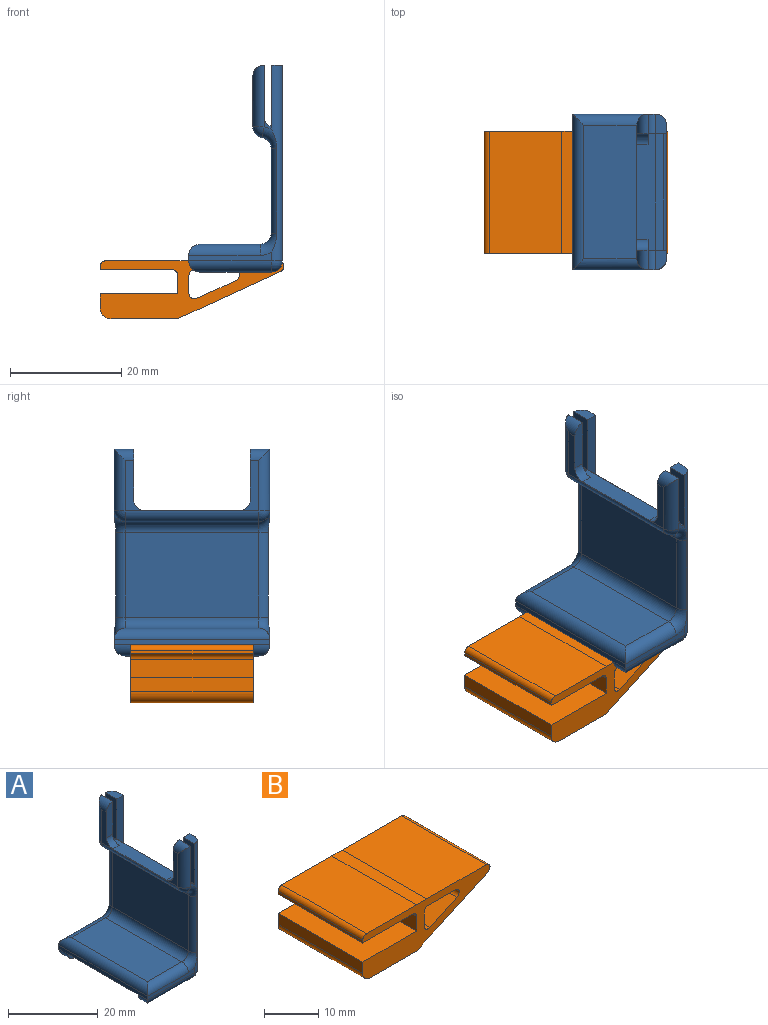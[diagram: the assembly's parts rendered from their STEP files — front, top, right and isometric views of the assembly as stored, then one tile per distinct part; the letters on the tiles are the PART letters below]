
ASSEMBLY  parts=2 mates=1
PART A: 61 faces, bbox 18.7x28x37.2 mm
  f0: plane 11x3.5mm, normal (-1,0,0), area 38.5mm2, adj f29,f31,f56,f58
  f1: plane 11x3.5mm, normal (-1,0,0), area 38.5mm2, adj f2,f24,f53,f54
  f2: cylinder r=2mm len=3.5mm, axis (0,1,0), area 8.5mm2, adj f1,f3,f17,f55
  f3: plane 2.41x1.3mm, normal (0,-1,0), area 1mm2, adj f2,f24,f25,f33
  f4: plane 2.41x1.3mm, normal (0,1,0), area 1mm2, adj f29,f30,f31,f38
  f5: plane 24x15.2mm, normal (-1,0,0), area 364.8mm2, adj f21,f22,f27,f28
  f6: plane 28x1mm, normal (-1,0,0), area 28mm2, adj f7,f9,f10,f19,f46,f50
  f7: plane 14.84x1.54mm, normal (0,-1,0), area 15.2mm2, adj f6,f18,f20,f24,f52
  f8: plane 35.2x24mm, normal (1,0,0), area 554.4mm2, adj f10,f24,f29,f45,f49,f53,f54,f56
  f9: plane 14.84x1.54mm, normal (0,1,0), area 15.2mm2, adj f6,f23,f26,f29,f48
  f10: plane 22x16.84mm, normal (0,0,-1), area 370.5mm2, adj f6,f8,f41,f43
  f11: plane 24x10.84mm, normal (0,0,1), area 260.2mm2, adj f18,f19,f22,f23
  f12: plane 21x3.3mm, normal (0,0,1), area 61.3mm2, adj f13,f16,f17,f39,f40,f55,f57,f59
  f13: plane 11x5.5mm, normal (1,0,0), area 32.8mm2, adj f12,f14,f31,f36,f38,f40,f57
  f14: plane 9x2mm, normal (0,-1,0), area 17.1mm2, adj f13,f16,f36,f40
  f15: plane 9x2mm, normal (0,1,0), area 17.1mm2, adj f16,f17,f32,f39
  f16: plane 24x9.06mm, normal (-1,0,0), area 30.2mm2, adj f12,f14,f15,f32,f33,f35,f36,f38
  f17: plane 11x5.5mm, normal (1,0,0), area 32.8mm2, adj f2,f12,f15,f32,f33,f39,f55
  f18: cylinder r=2mm len=12.84mm, axis (1,0,0), area 38.1mm2, adj f7,f11,f19,f20
  f19: cylinder r=2mm len=28mm, axis (0,-1,0), area 83.4mm2, adj f6,f11,f18,f23
  f20: torus R=4mm, axis (0,-1,0), area 10.8mm2, adj f7,f18,f21,f22,f24
  f21: cylinder r=2mm len=15.2mm, axis (0,0,1), area 31.8mm2, adj f5,f20,f24,f25
  f22: cylinder r=2mm len=24mm, axis (0,-1,0), area 75.4mm2, adj f5,f11,f20,f26
  f23: cylinder r=2mm len=12.84mm, axis (-1,0,0), area 38.1mm2, adj f9,f11,f19,f26
  f24: cylinder r=2mm len=35.2mm, axis (0,0,1), area 89.9mm2, adj f1,f3,f7,f8,f20,f21,f25,f51
  f25: torus R=4mm, axis (0,-1,0), area 9.3mm2, adj f3,f21,f24,f27,f34
  f26: torus R=4mm, axis (0,-1,0), area 10.8mm2, adj f9,f22,f23,f28,f29
  f27: cylinder r=2mm len=24mm, axis (0,1,0), area 67mm2, adj f5,f25,f30,f35
  f28: cylinder r=2mm len=15.2mm, axis (0,0,-1), area 31.8mm2, adj f5,f26,f29,f30
  f29: cylinder r=2mm len=35.2mm, axis (0,0,-1), area 89.9mm2, adj f0,f4,f8,f9,f26,f28,f30,f47
  f30: torus R=4mm, axis (0,-1,0), area 9.3mm2, adj f4,f27,f28,f29,f37
  f31: cylinder r=2mm len=3.5mm, axis (0,1,0), area 8.5mm2, adj f0,f4,f13,f57
  f32: cylinder r=2mm len=3.5mm, axis (0,-1,0), area 8.7mm2, adj f15,f16,f17,f33
  f33: cylinder r=2mm len=11.06mm, axis (0,0,-1), area 32.5mm2, adj f3,f16,f17,f32,f34
  f34: sphere r=2mm, area 5.6mm2, adj f25,f33,f35
  f35: cylinder r=2mm len=24mm, axis (0,1,0), area 67mm2, adj f16,f27,f34,f37
  f36: cylinder r=2mm len=3.5mm, axis (0,-1,0), area 8.7mm2, adj f13,f14,f16,f38
  f37: sphere r=2mm, area 5.7mm2, adj f30,f35,f38
  f38: cylinder r=2mm len=11.06mm, axis (0,0,1), area 32.5mm2, adj f4,f13,f16,f36,f37
  f39: cylinder r=2mm len=2mm, axis (1,0,0), area 6.3mm2, adj f12,f15,f16,f17
  f40: cylinder r=2mm len=2mm, axis (-1,0,0), area 6.3mm2, adj f12,f13,f14,f16
  f41: plane 16.84x2mm, normal (0,-1,0), area 32mm2, adj f10,f42,f45,f46
  f42: plane 12.84x1mm, normal (0,0,-1), area 12.8mm2, adj f41,f45,f46,f48
  f43: plane 16.84x2mm, normal (0,1,0), area 32mm2, adj f10,f44,f49,f50
  f44: plane 12.84x1mm, normal (0,0,-1), area 12.8mm2, adj f43,f49,f50,f52
  f45: cylinder r=2mm len=2mm, axis (0,1,0), area 3.1mm2, adj f8,f41,f42,f47
  f46: cylinder r=2mm len=3mm, axis (0,-1,0), area 7.1mm2, adj f6,f41,f42,f48
  f47: sphere r=2mm, area 6.3mm2, adj f29,f45,f48
  f48: cylinder r=2mm len=14.84mm, axis (-1,0,0), area 44.3mm2, adj f9,f42,f46,f47
  f49: cylinder r=2mm len=2mm, axis (0,1,0), area 3.1mm2, adj f8,f43,f44,f51
  f50: cylinder r=2mm len=3mm, axis (0,-1,0), area 7.1mm2, adj f6,f43,f44,f52
  f51: sphere r=2mm, area 6.3mm2, adj f24,f49,f52
  f52: cylinder r=2mm len=14.84mm, axis (1,0,0), area 44.3mm2, adj f7,f44,f50,f51
  f53: plane 3.5x2mm, normal (0,0,1), area 6.1mm2, adj f1,f8,f24,f54
  f54: plane 13.83x2mm, normal (0,1,0), area 24.1mm2, adj f1,f8,f53,f59,f60
  f55: plane 1.87x1.3mm, normal (0,1,0), area 0.7mm2, adj f2,f12,f17
  f56: plane 13.83x2mm, normal (0,-1,0), area 24.1mm2, adj f0,f8,f58,f59,f60
  f57: plane 1.87x1.3mm, normal (0,-1,0), area 0.7mm2, adj f12,f13,f31
  f58: plane 3.5x2mm, normal (0,0,1), area 6.1mm2, adj f0,f8,f29,f56
  f59: plane 21x1.41mm, normal (0.71,0,0.71), area 42mm2, adj f12,f54,f56,f60
  f60: cylinder r=2mm len=21mm, axis (0,1,0), area 33mm2, adj f8,f54,f56,f59
PART B: 22 faces, bbox 33.1x22x10.4 mm
  f0: plane 22x7.06mm, normal (-0.42,0,0.91), area 170.9mm2, adj f12,f13,f16,f18
  f1: plane 22x3.24mm, normal (1,0,0), area 71.3mm2, adj f12,f13,f16,f17
  f2: plane 22x13mm, normal (0,0,-1), area 286mm2, adj f10,f12,f13,f14
  f3: plane 22x3.3mm, normal (-1,0,0), area 72.6mm2, adj f12,f13,f14,f21
  f4: plane 22x2.5mm, normal (-1,0,0), area 55mm2, adj f12,f13,f20,f21
  f5: plane 22x12mm, normal (0,0,-1), area 264mm2, adj f6,f12,f13,f20
  f6: plane 22x18.51mm, normal (0.42,0,-0.91), area 448mm2, adj f5,f12,f13,f19
  f7: plane 22x15.42mm, normal (0,0,1), area 339.3mm2, adj f8,f12,f13,f19
  f8: plane 22x2.67mm, normal (0,0,1), area 58.7mm2, adj f7,f9,f12,f13
  f9: plane 22x13mm, normal (0,0,1), area 286mm2, adj f8,f12,f13,f15
  f10: plane 22x0.6mm, normal (-1,0,0), area 13.2mm2, adj f2,f12,f13,f15
  f11: plane 22x7.06mm, normal (0,0,-1), area 155.4mm2, adj f12,f13,f17,f18
  f12: plane 33.09x10.4mm, normal (0,-1,0), area 166.6mm2, adj f0,f1,f2,f3,f4,f5,f6,f7
  f13: plane 33.09x10.4mm, normal (0,1,0), area 166.6mm2, adj f0,f1,f2,f3,f4,f5,f6,f7
  f14: cylinder r=1mm len=22mm, axis (0,-1,0), area 34.6mm2, adj f2,f3,f12,f13
  f15: cylinder r=1mm len=22mm, axis (0,1,0), area 34.6mm2, adj f9,f10,f12,f13
  f16: cylinder r=1mm len=22mm, axis (0,-1,0), area 44mm2, adj f0,f1,f12,f13
  f17: cylinder r=1mm len=22mm, axis (0,1,0), area 34.6mm2, adj f1,f11,f12,f13
  f18: cylinder r=1mm len=22mm, axis (0,1,0), area 59.6mm2, adj f0,f11,f12,f13
  f19: cylinder r=1mm len=22mm, axis (0,1,0), area 59.6mm2, adj f6,f7,f12,f13
  f20: cylinder r=2mm len=22mm, axis (0,1,0), area 69.1mm2, adj f4,f5,f12,f13
  f21: plane 22x14mm, normal (0,0,1), area 308mm2, adj f3,f4,f12,f13
PLACE A t=(-71.44,-83.58,12.82)mm
PLACE B t=(-33.59,-14.09,4.84)mm
MATE fastened A.f10 <-> B.f7  axis (0,0,-1) through (-23.21,-25.09,9.82)mm
